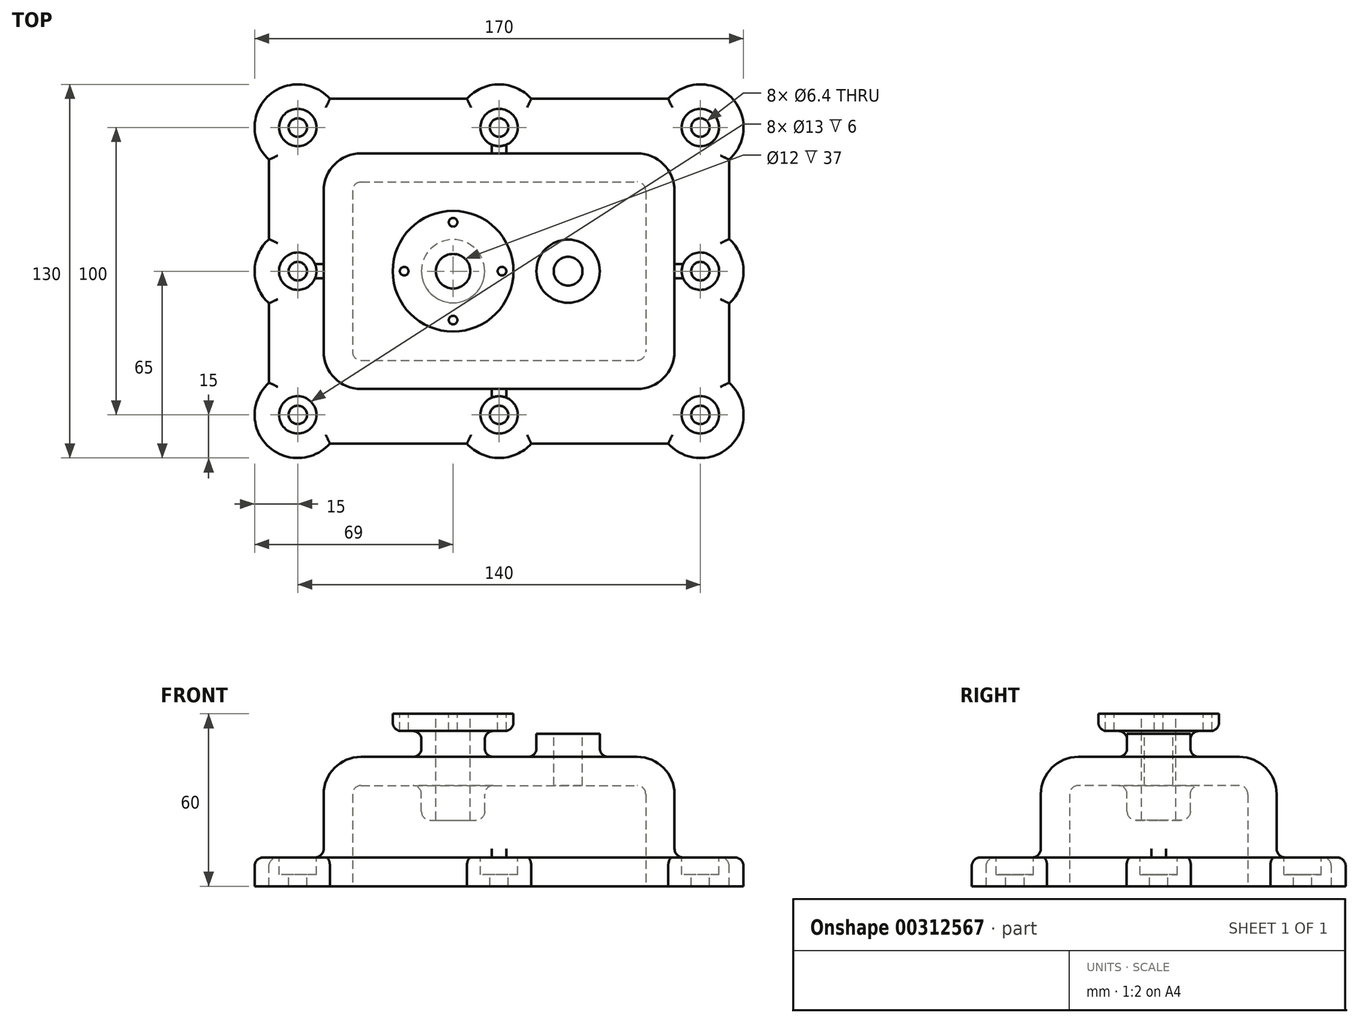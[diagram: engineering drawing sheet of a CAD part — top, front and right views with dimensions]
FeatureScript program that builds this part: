
annotation { "Feature Type Name" : "Feature", "Feature Type Description" : "" }
export const myFeature = defineFeature(function(context is Context, id is Id, definition is map)
    precondition{}
    {
        {
            var Q0;
            Q0=qCreatedBy(makeId("Top.planeOp"),FACE);
            var sketch = newSketch(context, id + "F0", { "sketchPlane" : qUnion([Q0])});
            skLineSegment(sketch, "E0.bottom", {"start": v(-80, 60) * mm, "end": v(80, 60) * mm});
            skLineSegment(sketch, "E0.top", {"start": v(-80, -60) * mm, "end": v(80, -60) * mm});
            skLineSegment(sketch, "E0.left", {"start": v(-80, 60) * mm, "end": v(-80, -60) * mm});
            skLineSegment(sketch, "E0.right", {"start": v(80, 60) * mm, "end": v(80, -60) * mm});
            skSolve(sketch);
        }
        {
            var Q0;
            Q0 = qSketchRegion(id + "F0", true);
            extrude(context, id + "F1", {"entities" : qUnion([Q0]), "depth" : 10 * mm});
        }
        {
            var Q0;
            Q0=makeQuery(id+"F1.opExtrude","CAP_FACE",FACE,{"disambiguationData":[OSD([sQuery(id+"F0.wireOp",EDGE,"E0.bottom"),sQuery(id+"F0.wireOp",EDGE,"E0.top"),sQuery(id+"F0.wireOp",EDGE,"E0.left"),sQuery(id+"F0.wireOp",EDGE,"E0.right")])],"isStart":false});
            var sketch = newSketch(context, id + "F2", { "sketchPlane" : qUnion([Q0])});
            skCircle(sketch, "E1", {"center": v(-70, 50) * mm, "radius": 15 * mm});
            skCircle(sketch, "E2", {"center": v(0, 50) * mm, "radius": 15 * mm});
            skCircle(sketch, "E3", {"center": v(70, 50) * mm, "radius": 15 * mm});
            skCircle(sketch, "E4", {"center": v(-70, 0) * mm, "radius": 15 * mm});
            skCircle(sketch, "E5", {"center": v(70, 0) * mm, "radius": 15 * mm});
            skCircle(sketch, "E6", {"center": v(-70, -50) * mm, "radius": 15 * mm});
            skCircle(sketch, "E7", {"center": v(0, -50) * mm, "radius": 15 * mm});
            skCircle(sketch, "E8", {"center": v(70, -50) * mm, "radius": 15 * mm});
            skSolve(sketch);
        }
        {
            var Q0;
            Q0 = qSketchRegion(id + "F2", true);
            var Q1;
            Q1=qCreatedBy(makeId("Top.planeOp"),FACE);
            extrude(context, id + "F3", {"entities" : qUnion([Q0]), "operationType" : NewBodyOperationType.ADD, "endBound" : BoundingType.UP_TO_SURFACE, "oppositeDirection" : true, "endBoundEntityFace" : qUnion([Q1]), "depth" : 25 * mm});
        }
        {
            var Q0;
            Q0=qCreatedBy(makeId("Top.planeOp"),FACE);
            var sketch = newSketch(context, id + "F4", { "sketchPlane" : qUnion([Q0])});
            skLineSegment(sketch, "E9.bottom", {"start": v(-48, 41) * mm, "end": v(48, 41) * mm});
            skLineSegment(sketch, "E9.top", {"start": v(-48, -41) * mm, "end": v(48, -41) * mm});
            skLineSegment(sketch, "E9.left", {"start": v(-61, 28) * mm, "end": v(-61, -28) * mm});
            skLineSegment(sketch, "E9.right", {"start": v(61, 28) * mm, "end": v(61, -28) * mm});
            skPoint(sketch, "E10.visualSharp", {"position": v(-61, 41) * mm});
            skArc(sketch, "E10.filletArc", {"start": v(-48, 41) * mm, "mid": v(-57.2, 37.2) * mm, "end": v(-61, 28) * mm});
            skPoint(sketch, "E11.visualSharp", {"position": v(61, 41) * mm});
            skArc(sketch, "E11.filletArc", {"start": v(61, 28) * mm, "mid": v(57.2, 37.2) * mm, "end": v(48, 41) * mm});
            skPoint(sketch, "E12.visualSharp", {"position": v(-61, -41) * mm});
            skArc(sketch, "E12.filletArc", {"start": v(-61, -28) * mm, "mid": v(-57.2, -37.2) * mm, "end": v(-48, -41) * mm});
            skPoint(sketch, "E13.visualSharp", {"position": v(61, -41) * mm});
            skArc(sketch, "E13.filletArc", {"start": v(48, -41) * mm, "mid": v(57.2, -37.2) * mm, "end": v(61, -28) * mm});
            skSolve(sketch);
        }
        {
            var Q0;
            Q0 = qSketchRegion(id + "F4", true);
            extrude(context, id + "F5", {"entities" : qUnion([Q0]), "operationType" : NewBodyOperationType.ADD, "depth" : 45 * mm});
        }
        {
            var Q0;
            Q0=qCreatedBy(makeId("Top.planeOp"),FACE);
            var sketch = newSketch(context, id + "F6", { "sketchPlane" : qUnion([Q0])});
            skArc(sketch, "E14.0", {"start": v(-48, 31) * mm, "mid": v(-50.12, 30.12) * mm, "end": v(-51, 28) * mm});
            skLineSegment(sketch, "E14.1", {"start": v(-51, 28) * mm, "end": v(-51, -28) * mm});
            skLineSegment(sketch, "E14.2", {"start": v(-48, 31) * mm, "end": v(48, 31) * mm});
            skArc(sketch, "E14.3", {"start": v(-51, -28) * mm, "mid": v(-50.12, -30.12) * mm, "end": v(-48, -31) * mm});
            skArc(sketch, "E14.4", {"start": v(51, 28) * mm, "mid": v(50.12, 30.12) * mm, "end": v(48, 31) * mm});
            skLineSegment(sketch, "E14.5", {"start": v(51, 28) * mm, "end": v(51, -28) * mm});
            skArc(sketch, "E14.6", {"start": v(48, -31) * mm, "mid": v(50.12, -30.12) * mm, "end": v(51, -28) * mm});
            skLineSegment(sketch, "E14.7", {"start": v(-48, -31) * mm, "end": v(48, -31) * mm});
            skSolve(sketch);
        }
        {
            var Q0;
            Q0 = qSketchRegion(id + "F6", true);
            extrude(context, id + "F7", {"entities" : qUnion([Q0]), "depth" : 35 * mm});
        }
        {
            var Q0;
            Q0=makeQuery(id+"F7.opExtrude","SWEPT_BODY",BODY,{"disambiguationData":[OSD([sQuery(id+"F6.wireOp",EDGE,"E14.0"),sQuery(id+"F6.wireOp",EDGE,"E14.1"),sQuery(id+"F6.wireOp",EDGE,"E14.2"),sQuery(id+"F6.wireOp",EDGE,"E14.3"),sQuery(id+"F6.wireOp",EDGE,"E14.4"),sQuery(id+"F6.wireOp",EDGE,"E14.5"),sQuery(id+"F6.wireOp",EDGE,"E14.6"),sQuery(id+"F6.wireOp",EDGE,"E14.7")])]});
            var Q1;
            Q1=makeQuery(id+"F1.opExtrude","SWEPT_BODY",BODY,{"disambiguationData":[OSD([sQuery(id+"F0.wireOp",EDGE,"E0.bottom"),sQuery(id+"F0.wireOp",EDGE,"E0.top"),sQuery(id+"F0.wireOp",EDGE,"E0.left"),sQuery(id+"F0.wireOp",EDGE,"E0.right")])]});
            booleanBodies(context, id + "F8", {"operationType" : BooleanOperationType.SUBTRACTION, "tools" : qUnion([Q0]), "targets" : qUnion([Q1])});
        }
        {
            var Q0;
            Q0=qCreatedBy(makeId("Top.planeOp"),FACE);
            cPlane(context, id + "F9", {"entities" : qUnion([Q0]), "cplaneType" : CPlaneType.OFFSET, "offset" : 60 * mm, "width" : 150 * mm, "height" : 150 * mm});
        }
        {
            var Q0;
            Q0=qCreatedBy(id+"F9.planeOp",FACE);
            var sketch = newSketch(context, id + "F10", { "sketchPlane" : qUnion([Q0])});
            skCircle(sketch, "E15", {"center": v(-16, 0) * mm, "radius": 21 * mm});
            skSolve(sketch);
        }
        {
            var Q0;
            Q0 = qSketchRegion(id + "F10", true);
            extrude(context, id + "F11", {"entities" : qUnion([Q0]), "oppositeDirection" : true, "depth" : 6 * mm});
        }
        {
            var Q0;
            Q0=qCreatedBy(id+"F9.planeOp",FACE);
            var sketch = newSketch(context, id + "F12", { "sketchPlane" : qUnion([Q0])});
            skCircle(sketch, "E16", {"center": v(-16, 0) * mm, "radius": 11 * mm});
            skSolve(sketch);
        }
        {
            var Q0;
            Q0=makeQuery(id+"F8.opBoolean","COPY",FACE,{"derivedFrom":makeQuery(id+"F7.opExtrude","CAP_FACE",FACE,{"disambiguationData":[OSD([sQuery(id+"F6.wireOp",EDGE,"E14.0"),sQuery(id+"F6.wireOp",EDGE,"E14.1"),sQuery(id+"F6.wireOp",EDGE,"E14.2"),sQuery(id+"F6.wireOp",EDGE,"E14.3"),sQuery(id+"F6.wireOp",EDGE,"E14.4"),sQuery(id+"F6.wireOp",EDGE,"E14.5"),sQuery(id+"F6.wireOp",EDGE,"E14.6"),sQuery(id+"F6.wireOp",EDGE,"E14.7")])],"isStart":false})});
            cPlane(context, id + "F13", {"entities" : qUnion([Q0]), "cplaneType" : CPlaneType.OFFSET, "offset" : 12 * mm, "width" : 150 * mm, "height" : 150 * mm});
        }
        {
            var Q0;
            Q0 = qSketchRegion(id + "F12", true);
            var Q1;
            Q1=qCreatedBy(id+"F13.planeOp",FACE);
            extrude(context, id + "F14", {"entities" : qUnion([Q0]), "endBound" : BoundingType.UP_TO_SURFACE, "oppositeDirection" : true, "endBoundEntityFace" : qUnion([Q1]), "depth" : 25 * mm});
        }
        {
            var Q0;
            Q0=makeQuery(id+"F1.opExtrude","SWEPT_BODY",BODY,{"disambiguationData":[OSD([sQuery(id+"F0.wireOp",EDGE,"E0.bottom"),sQuery(id+"F0.wireOp",EDGE,"E0.top"),sQuery(id+"F0.wireOp",EDGE,"E0.left"),sQuery(id+"F0.wireOp",EDGE,"E0.right")])]});
            var Q1;
            Q1=makeQuery(id+"F11.opExtrude","SWEPT_BODY",BODY,{"disambiguationData":[OSD([sQuery(id+"F10.wireOp",EDGE,"E15")])]});
            var Q2;
            Q2=makeQuery(id+"F14.opExtrude","SWEPT_BODY",BODY,{"disambiguationData":[OSD([sQuery(id+"F12.wireOp",EDGE,"E16")])]});
            booleanBodies(context, id + "F15", {"operationType" : BooleanOperationType.UNION, "tools" : qUnion([Q0, Q1, Q2])});
        }
        {
            var Q0;
            Q0=qCreatedBy(id+"F9.planeOp",FACE);
            var sketch = newSketch(context, id + "F16", { "sketchPlane" : qUnion([Q0])});
            skPoint(sketch, "E17", {"position": v(-16, 0) * mm});
            skSolve(sketch);
        }
        {
            var Q0;
            Q0=sQuery(id+"F16.wireOp",VERTEX,"E17");
            var Q1;
            Q1=makeQuery(id+"F1.opExtrude","SWEPT_BODY",BODY,{"disambiguationData":[OSD([sQuery(id+"F0.wireOp",EDGE,"E0.bottom"),sQuery(id+"F0.wireOp",EDGE,"E0.top"),sQuery(id+"F0.wireOp",EDGE,"E0.left"),sQuery(id+"F0.wireOp",EDGE,"E0.right")])]});
            hole(context, id + "F17", {"style" : HoleStyle.SIMPLE, "endStyle" : HoleEndStyle.THROUGH, "holeDiameter" : 12 * mm, "tappedDepth" : 12 * mm, "tapClearance" : 3, "locations" : qUnion([Q0]), "scope" : qUnion([Q1])});
        }
        {
            var Q0;
            Q0=qCreatedBy(makeId("Top.planeOp"),FACE);
            cPlane(context, id + "F18", {"entities" : qUnion([Q0]), "cplaneType" : CPlaneType.OFFSET, "offset" : 53 * mm, "width" : 150 * mm, "height" : 150 * mm});
        }
        {
            var Q0;
            Q0=qCreatedBy(id+"F18.planeOp",FACE);
            var sketch = newSketch(context, id + "F19", { "sketchPlane" : qUnion([Q0])});
            skCircle(sketch, "E18", {"center": v(24, 0) * mm, "radius": 11 * mm});
            skSolve(sketch);
        }
        {
            var Q0;
            Q0 = qSketchRegion(id + "F19", true);
            var Q1;
            Q1=makeQuery(id+"F8.opBoolean","COPY",FACE,{"derivedFrom":makeQuery(id+"F7.opExtrude","CAP_FACE",FACE,{"disambiguationData":[OSD([sQuery(id+"F6.wireOp",EDGE,"E14.0"),sQuery(id+"F6.wireOp",EDGE,"E14.1"),sQuery(id+"F6.wireOp",EDGE,"E14.2"),sQuery(id+"F6.wireOp",EDGE,"E14.3"),sQuery(id+"F6.wireOp",EDGE,"E14.4"),sQuery(id+"F6.wireOp",EDGE,"E14.5"),sQuery(id+"F6.wireOp",EDGE,"E14.6"),sQuery(id+"F6.wireOp",EDGE,"E14.7")])],"isStart":false})});
            extrude(context, id + "F20", {"entities" : qUnion([Q0]), "operationType" : NewBodyOperationType.ADD, "endBound" : BoundingType.UP_TO_SURFACE, "oppositeDirection" : true, "endBoundEntityFace" : qUnion([Q1]), "depth" : 25 * mm});
        }
        {
            var Q0;
            Q0=qCreatedBy(id+"F18.planeOp",FACE);
            var sketch = newSketch(context, id + "F21", { "sketchPlane" : qUnion([Q0])});
            skPoint(sketch, "E19", {"position": v(24, 0) * mm});
            skSolve(sketch);
        }
        {
            var Q0;
            Q0=sQuery(id+"F21.wireOp",VERTEX,"E19");
            var Q1;
            Q1=makeQuery(id+"F1.opExtrude","SWEPT_BODY",BODY,{"disambiguationData":[OSD([sQuery(id+"F0.wireOp",EDGE,"E0.bottom"),sQuery(id+"F0.wireOp",EDGE,"E0.top"),sQuery(id+"F0.wireOp",EDGE,"E0.left"),sQuery(id+"F0.wireOp",EDGE,"E0.right")])]});
            hole(context, id + "F22", {"style" : HoleStyle.SIMPLE, "endStyle" : HoleEndStyle.THROUGH, "holeDiameter" : 10 * mm, "tappedDepth" : 12 * mm, "tapClearance" : 3, "locations" : qUnion([Q0]), "scope" : qUnion([Q1])});
        }
        {
            var Q0;
            Q0=qCreatedBy(makeId("Top.planeOp"),FACE);
            cPlane(context, id + "F23", {"entities" : qUnion([Q0]), "cplaneType" : CPlaneType.OFFSET, "offset" : 10 * mm, "width" : 150 * mm, "height" : 150 * mm});
        }
        {
            var Q0;
            Q0=qCreatedBy(id+"F23.planeOp",FACE);
            var sketch = newSketch(context, id + "F24", { "sketchPlane" : qUnion([Q0])});
            skPoint(sketch, "E20", {"position": v(70, 50) * mm});
            skPoint(sketch, "E21", {"position": v(0, 50) * mm});
            skPoint(sketch, "E22", {"position": v(-70, 50) * mm});
            skPoint(sketch, "E23", {"position": v(-70, 0) * mm});
            skPoint(sketch, "E24", {"position": v(-70, -50) * mm});
            skPoint(sketch, "E25", {"position": v(0, -50) * mm});
            skPoint(sketch, "E26", {"position": v(70, -50) * mm});
            skPoint(sketch, "E27", {"position": v(70, 0) * mm});
            skSolve(sketch);
        }
        {
            var Q0;
            Q0=sQuery(id+"F24.wireOp",VERTEX,"E22");
            var Q1;
            Q1=sQuery(id+"F24.wireOp",VERTEX,"E23");
            var Q2;
            Q2=sQuery(id+"F24.wireOp",VERTEX,"E24");
            var Q3;
            Q3=sQuery(id+"F24.wireOp",VERTEX,"E25");
            var Q4;
            Q4=sQuery(id+"F24.wireOp",VERTEX,"E26");
            var Q5;
            Q5=sQuery(id+"F24.wireOp",VERTEX,"E27");
            var Q6;
            Q6=sQuery(id+"F24.wireOp",VERTEX,"E20");
            var Q7;
            Q7=sQuery(id+"F24.wireOp",VERTEX,"E21");
            var Q8;
            Q8=makeQuery(id+"F1.opExtrude","SWEPT_BODY",BODY,{"disambiguationData":[OSD([sQuery(id+"F0.wireOp",EDGE,"E0.bottom"),sQuery(id+"F0.wireOp",EDGE,"E0.top"),sQuery(id+"F0.wireOp",EDGE,"E0.left"),sQuery(id+"F0.wireOp",EDGE,"E0.right")])]});
            hole(context, id + "F25", {"style" : HoleStyle.C_BORE, "endStyle" : HoleEndStyle.THROUGH, "holeDiameter" : 6.4 * mm, "cBoreDiameter" : 13 * mm, "cBoreDepth" : 6 * mm, "tappedDepth" : 12 * mm, "tapClearance" : 3, "locations" : qUnion([Q0, Q1, Q2, Q3, Q4, Q5, Q6, Q7]), "scope" : qUnion([Q8])});
        }
        {
            var Q0;
            Q0=makeQuery(id+"F5.opExtrude","CAP_EDGE",EDGE,{"disambiguationData":[OSD([sQuery(id+"F4.wireOp",EDGE,"E9.right")])],"isStart":false});
            fillet(context, id + "F26", {"entities" : qUnion([Q0]), "radius" : 13 * mm, "tangentPropagation" : true, "allowEdgeOverflow" : false});
        }
        {
            var Q0;
            Q0=makeQuery(id+"F20.boolean.opBoolean","INTERSECT",EDGE,{"derivedFrom":[makeQuery(id+"F5.opExtrude","CAP_FACE",FACE,{"disambiguationData":[OSD([sQuery(id+"F4.wireOp",EDGE,"E9.bottom"),sQuery(id+"F4.wireOp",EDGE,"E9.top"),sQuery(id+"F4.wireOp",EDGE,"E9.left"),sQuery(id+"F4.wireOp",EDGE,"E9.right"),sQuery(id+"F4.wireOp",EDGE,"E10.filletArc"),sQuery(id+"F4.wireOp",EDGE,"E11.filletArc"),sQuery(id+"F4.wireOp",EDGE,"E12.filletArc"),sQuery(id+"F4.wireOp",EDGE,"E13.filletArc")])],"isStart":false}),makeQuery(id+"F20.opExtrude","SWEPT_FACE",FACE,{"disambiguationData":[OSD([sQuery(id+"F19.wireOp",EDGE,"E18")])]})]});
            var Q1;
            Q1=makeQuery(id+"F11.opExtrude","CAP_EDGE",EDGE,{"disambiguationData":[OSD([sQuery(id+"F10.wireOp",EDGE,"E15")])],"isStart":false});
            var Q2;
            Q2=makeQuery(id+"F15.opBoolean","INTERSECT",EDGE,{"derivedFrom":[makeQuery(id+"F5.opExtrude","CAP_FACE",FACE,{"disambiguationData":[OSD([sQuery(id+"F4.wireOp",EDGE,"E9.bottom"),sQuery(id+"F4.wireOp",EDGE,"E9.top"),sQuery(id+"F4.wireOp",EDGE,"E9.left"),sQuery(id+"F4.wireOp",EDGE,"E9.right"),sQuery(id+"F4.wireOp",EDGE,"E10.filletArc"),sQuery(id+"F4.wireOp",EDGE,"E11.filletArc"),sQuery(id+"F4.wireOp",EDGE,"E12.filletArc"),sQuery(id+"F4.wireOp",EDGE,"E13.filletArc")])],"isStart":false}),makeQuery(id+"F14.opExtrude","SWEPT_FACE",FACE,{"disambiguationData":[OSD([sQuery(id+"F12.wireOp",EDGE,"E16")])]})]});
            var Q3;
            Q3=makeQuery(id+"F15.opBoolean","INTERSECT",EDGE,{"derivedFrom":[makeQuery(id+"F11.opExtrude","CAP_FACE",FACE,{"disambiguationData":[OSD([sQuery(id+"F10.wireOp",EDGE,"E15")])],"isStart":false}),makeQuery(id+"F14.opExtrude","SWEPT_FACE",FACE,{"disambiguationData":[OSD([sQuery(id+"F12.wireOp",EDGE,"E16")])]})]});
            fillet(context, id + "F27", {"entities" : qUnion([Q0, Q1, Q2, Q3]), "radius" : 3 * mm, "tangentPropagation" : true, "allowEdgeOverflow" : false});
        }
        {
            var Q0;
            Q0=makeQuery(id+"F5.boolean.opBoolean","INTERSECT",EDGE,{"derivedFrom":[makeQuery(id+"F3.boolean.opBoolean","MERGE",FACE,{"derivedFrom":[makeQuery(id+"F1.opExtrude","CAP_FACE",FACE,{"disambiguationData":[OSD([sQuery(id+"F0.wireOp",EDGE,"E0.bottom"),sQuery(id+"F0.wireOp",EDGE,"E0.top"),sQuery(id+"F0.wireOp",EDGE,"E0.left"),sQuery(id+"F0.wireOp",EDGE,"E0.right")])],"isStart":false}),makeQuery(id+"F3.opExtrude","CAP_FACE",FACE,{"disambiguationData":[OSD([sQuery(id+"F2.wireOp",EDGE,"E1")])],"isStart":true}),makeQuery(id+"F3.opExtrude","CAP_FACE",FACE,{"disambiguationData":[OSD([sQuery(id+"F2.wireOp",EDGE,"E2")])],"isStart":true}),makeQuery(id+"F3.opExtrude","CAP_FACE",FACE,{"disambiguationData":[OSD([sQuery(id+"F2.wireOp",EDGE,"E3")])],"isStart":true}),makeQuery(id+"F3.opExtrude","CAP_FACE",FACE,{"disambiguationData":[OSD([sQuery(id+"F2.wireOp",EDGE,"E4")])],"isStart":true}),makeQuery(id+"F3.opExtrude","CAP_FACE",FACE,{"disambiguationData":[OSD([sQuery(id+"F2.wireOp",EDGE,"E5")])],"isStart":true}),makeQuery(id+"F3.opExtrude","CAP_FACE",FACE,{"disambiguationData":[OSD([sQuery(id+"F2.wireOp",EDGE,"E6")])],"isStart":true}),makeQuery(id+"F3.opExtrude","CAP_FACE",FACE,{"disambiguationData":[OSD([sQuery(id+"F2.wireOp",EDGE,"E7")])],"isStart":true}),makeQuery(id+"F3.opExtrude","CAP_FACE",FACE,{"disambiguationData":[OSD([sQuery(id+"F2.wireOp",EDGE,"E8")])],"isStart":true})]}),makeQuery(id+"F5.opExtrude","SWEPT_FACE",FACE,{"disambiguationData":[OSD([sQuery(id+"F4.wireOp",EDGE,"E9.top")])]})]});
            var Q1;
            Q1=makeQuery(id+"F3.opExtrude","CAP_EDGE",EDGE,{"disambiguationData":[OSD([sQuery(id+"F2.wireOp",EDGE,"E8")])],"isStart":true});
            var Q2;
            {var subQ1=sQuery(id+"F0.wireOp",EDGE,"E0.top");var subQ2=sQuery(id+"F2.wireOp",EDGE,"E8");Q2=makeQuery(id+"F3.boolean.opBoolean","SPLIT",EDGE,{"disambiguationData":[TD([makeQuery(id+"F3.opExtrude","SWEPT_FACE",FACE,{"disambiguationData":[OSD([subQ2])]})])],"derivedFrom":makeQuery(id+"F1.opExtrude","CAP_EDGE",EDGE,{"disambiguationData":[OSD([subQ1])],"isStart":false})});}
            var Q3;
            Q3=makeQuery(id+"F3.opExtrude","CAP_EDGE",EDGE,{"disambiguationData":[OSD([sQuery(id+"F2.wireOp",EDGE,"E7")])],"isStart":true});
            var Q4;
            {var subQ0=sQuery(id+"F2.wireOp",EDGE,"E6");var subQ2=sQuery(id+"F0.wireOp",EDGE,"E0.top");Q4=makeQuery(id+"F3.boolean.opBoolean","SPLIT",EDGE,{"disambiguationData":[TD([makeQuery(id+"F3.opExtrude","SWEPT_FACE",FACE,{"disambiguationData":[OSD([subQ0])]})])],"derivedFrom":makeQuery(id+"F1.opExtrude","CAP_EDGE",EDGE,{"disambiguationData":[OSD([subQ2])],"isStart":false})});}
            var Q5;
            Q5=makeQuery(id+"F3.opExtrude","CAP_EDGE",EDGE,{"disambiguationData":[OSD([sQuery(id+"F2.wireOp",EDGE,"E6")])],"isStart":true});
            var Q6;
            {var subQ0=sQuery(id+"F2.wireOp",EDGE,"E6");var subQ2=sQuery(id+"F0.wireOp",EDGE,"E0.left");Q6=makeQuery(id+"F3.boolean.opBoolean","SPLIT",EDGE,{"disambiguationData":[TD([makeQuery(id+"F3.opExtrude","SWEPT_FACE",FACE,{"disambiguationData":[OSD([subQ0])]})])],"derivedFrom":makeQuery(id+"F1.opExtrude","CAP_EDGE",EDGE,{"disambiguationData":[OSD([subQ2])],"isStart":false})});}
            var Q7;
            Q7=makeQuery(id+"F3.opExtrude","CAP_EDGE",EDGE,{"disambiguationData":[OSD([sQuery(id+"F2.wireOp",EDGE,"E4")])],"isStart":true});
            var Q8;
            {var subQ1=sQuery(id+"F0.wireOp",EDGE,"E0.left");var subQ2=sQuery(id+"F2.wireOp",EDGE,"E1");Q8=makeQuery(id+"F3.boolean.opBoolean","SPLIT",EDGE,{"disambiguationData":[TD([makeQuery(id+"F3.opExtrude","SWEPT_FACE",FACE,{"disambiguationData":[OSD([subQ2])]})])],"derivedFrom":makeQuery(id+"F1.opExtrude","CAP_EDGE",EDGE,{"disambiguationData":[OSD([subQ1])],"isStart":false})});}
            var Q9;
            Q9=makeQuery(id+"F3.opExtrude","CAP_EDGE",EDGE,{"disambiguationData":[OSD([sQuery(id+"F2.wireOp",EDGE,"E1")])],"isStart":true});
            var Q10;
            {var subQ1=sQuery(id+"F0.wireOp",EDGE,"E0.bottom");var subQ2=sQuery(id+"F2.wireOp",EDGE,"E1");Q10=makeQuery(id+"F3.boolean.opBoolean","SPLIT",EDGE,{"disambiguationData":[TD([makeQuery(id+"F3.opExtrude","SWEPT_FACE",FACE,{"disambiguationData":[OSD([subQ2])]})])],"derivedFrom":makeQuery(id+"F1.opExtrude","CAP_EDGE",EDGE,{"disambiguationData":[OSD([subQ1])],"isStart":false})});}
            var Q11;
            Q11=makeQuery(id+"F3.opExtrude","CAP_EDGE",EDGE,{"disambiguationData":[OSD([sQuery(id+"F2.wireOp",EDGE,"E2")])],"isStart":true});
            var Q12;
            {var subQ0=sQuery(id+"F2.wireOp",EDGE,"E3");var subQ2=sQuery(id+"F0.wireOp",EDGE,"E0.bottom");Q12=makeQuery(id+"F3.boolean.opBoolean","SPLIT",EDGE,{"disambiguationData":[TD([makeQuery(id+"F3.opExtrude","SWEPT_FACE",FACE,{"disambiguationData":[OSD([subQ0])]})])],"derivedFrom":makeQuery(id+"F1.opExtrude","CAP_EDGE",EDGE,{"disambiguationData":[OSD([subQ2])],"isStart":false})});}
            var Q13;
            Q13=makeQuery(id+"F3.opExtrude","CAP_EDGE",EDGE,{"disambiguationData":[OSD([sQuery(id+"F2.wireOp",EDGE,"E3")])],"isStart":true});
            var Q14;
            {var subQ1=sQuery(id+"F2.wireOp",EDGE,"E3");var subQ2=sQuery(id+"F0.wireOp",EDGE,"E0.right");Q14=makeQuery(id+"F3.boolean.opBoolean","SPLIT",EDGE,{"disambiguationData":[TD([makeQuery(id+"F3.opExtrude","SWEPT_FACE",FACE,{"disambiguationData":[OSD([subQ1])]})])],"derivedFrom":makeQuery(id+"F1.opExtrude","CAP_EDGE",EDGE,{"disambiguationData":[OSD([subQ2])],"isStart":false})});}
            var Q15;
            Q15=makeQuery(id+"F3.opExtrude","CAP_EDGE",EDGE,{"disambiguationData":[OSD([sQuery(id+"F2.wireOp",EDGE,"E5")])],"isStart":true});
            var Q16;
            {var subQ1=sQuery(id+"F0.wireOp",EDGE,"E0.right");var subQ2=sQuery(id+"F2.wireOp",EDGE,"E8");Q16=makeQuery(id+"F3.boolean.opBoolean","SPLIT",EDGE,{"disambiguationData":[TD([makeQuery(id+"F3.opExtrude","SWEPT_FACE",FACE,{"disambiguationData":[OSD([subQ2])]})])],"derivedFrom":makeQuery(id+"F1.opExtrude","CAP_EDGE",EDGE,{"disambiguationData":[OSD([subQ1])],"isStart":false})});}
            fillet(context, id + "F28", {"entities" : qUnion([Q0, Q1, Q2, Q3, Q4, Q5, Q6, Q7, Q8, Q9, Q10, Q11, Q12, Q13, Q14, Q15, Q16]), "radius" : 3 * mm, "tangentPropagation" : true, "allowEdgeOverflow" : false});
        }
        {
            var Q0;
            Q0=makeQuery(id+"F8.opBoolean","COPY",EDGE,{"derivedFrom":makeQuery(id+"F7.opExtrude","CAP_EDGE",EDGE,{"disambiguationData":[OSD([sQuery(id+"F6.wireOp",EDGE,"E14.5")])],"isStart":false})});
            var Q1;
            Q1=makeQuery(id+"F15.opBoolean","INTERSECT",EDGE,{"derivedFrom":[makeQuery(id+"F8.opBoolean","COPY",FACE,{"derivedFrom":makeQuery(id+"F7.opExtrude","CAP_FACE",FACE,{"disambiguationData":[OSD([sQuery(id+"F6.wireOp",EDGE,"E14.0"),sQuery(id+"F6.wireOp",EDGE,"E14.1"),sQuery(id+"F6.wireOp",EDGE,"E14.2"),sQuery(id+"F6.wireOp",EDGE,"E14.3"),sQuery(id+"F6.wireOp",EDGE,"E14.4"),sQuery(id+"F6.wireOp",EDGE,"E14.5"),sQuery(id+"F6.wireOp",EDGE,"E14.6"),sQuery(id+"F6.wireOp",EDGE,"E14.7")])],"isStart":false})}),makeQuery(id+"F14.opExtrude","SWEPT_FACE",FACE,{"disambiguationData":[OSD([sQuery(id+"F12.wireOp",EDGE,"E16")])]})]});
            var Q2;
            Q2=makeQuery(id+"F14.opExtrude","CAP_EDGE",EDGE,{"disambiguationData":[OSD([sQuery(id+"F12.wireOp",EDGE,"E16")])],"isStart":false});
            fillet(context, id + "F29", {"entities" : qUnion([Q0, Q1, Q2]), "radius" : 3 * mm, "tangentPropagation" : true, "allowEdgeOverflow" : false});
        }
        {
            var Q0;
            Q0=qCreatedBy(id+"F9.planeOp",FACE);
            var sketch = newSketch(context, id + "F30", { "sketchPlane" : qUnion([Q0])});
            skCircle(sketch, "E28", {"center": v(-16, 0) * mm, "radius": 17 * mm, "construction": true});
            skLineSegment(sketch, "E29", {"start": v(-16, 27.25) * mm, "end": v(-16, -26.56) * mm, "construction": true});
            skLineSegment(sketch, "E30", {"start": v(-43.92, 0) * mm, "end": v(10.12, 0) * mm, "construction": true});
            skPoint(sketch, "E31", {"position": v(-16, 17) * mm});
            skPoint(sketch, "E32", {"position": v(-33, 0) * mm});
            skPoint(sketch, "E33", {"position": v(-16, -17) * mm});
            skPoint(sketch, "E34", {"position": v(1, 0) * mm});
            skSolve(sketch);
        }
        {
            var Q0;
            Q0=sQuery(id+"F30.wireOp",VERTEX,"E31");
            var Q1;
            Q1=sQuery(id+"F30.wireOp",VERTEX,"E32");
            var Q2;
            Q2=sQuery(id+"F30.wireOp",VERTEX,"E33");
            var Q3;
            Q3=sQuery(id+"F30.wireOp",VERTEX,"E34");
            var Q4;
            Q4=makeQuery(id+"F1.opExtrude","SWEPT_BODY",BODY,{"disambiguationData":[OSD([sQuery(id+"F0.wireOp",EDGE,"E0.bottom"),sQuery(id+"F0.wireOp",EDGE,"E0.top"),sQuery(id+"F0.wireOp",EDGE,"E0.left"),sQuery(id+"F0.wireOp",EDGE,"E0.right")])]});
            hole(context, id + "F31", {"style" : HoleStyle.SIMPLE, "endStyle" : HoleEndStyle.BLIND, "holeDiameter" : 3 * mm, "holeDepth" : 12 * mm, "tappedDepth" : 12 * mm, "tapClearance" : 3, "locations" : qUnion([Q0, Q1, Q2, Q3]), "scope" : qUnion([Q4])});
        }
    });
